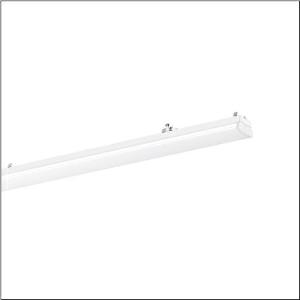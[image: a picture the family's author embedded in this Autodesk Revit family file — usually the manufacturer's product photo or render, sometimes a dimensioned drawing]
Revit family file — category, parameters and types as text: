
# Revit family: licross_r__11_recessed_opal_mo_51tl1d7n44xg_4ee8
name_source: partatom
category: Lighting Fixtures
units: mm (PartAtom-declared; Revit-internal decimal feet)

## family parameters
Cut with Voids When Loaded = No
Host = Face
Light Source = No
Part Type = Normal
Room Calculation Point = No
Round Connector Dimension = Use Diameter
Shared = No

## types (1)
- Licross® 11 recessed opal MO (1 x LED, 4480 lm, 24.8 W, 4000K)
    Apparent Load = 25 VA
    CIE Flux Codes = 44 73 91 87 100
    Color Rendering = 80
    Color Temperature = 4000K
    Default Elevation = 1800 mm
    Description = Licross® 11 recessed opal MO, luminaire insert, of sheet steel, coil coated, white, length: 1.500mm, width: 76mm, height: 87mm, LED rated luminous flux: 4.480lm, light colour: 840, control gear: ON/OFF, with plug, 3-pole, with phase selection, mains connection: 220..240V, AC, 50/60Hz, rated input power: 25W, halogen-free wiring, primary optical cover: cover, of PMMA, light emission: direct with ceiling illumination distribution, primary light characteristic: symmetric, protection rating (complete): IP40, insulation class (complete): insulation class I (protective earthing), certification: CE, ENEC, VDE, UKCA, protection symbol: D if used in an environment without relevant dust loads with corresponding accessories, impact resistance: IK06, permissible ambient temperature for indoor applications: -35..+45°C, corresponds to IFS (International Featured Standards) requirements for safety and quality in the food industry, reducing of maximum allowable ambient temperature of 5°C with ceiling mounting, packaging unit: 1 piece
    Height = 83 mm
    Lamp = 1 x LED
    Lamp Light Flux = 4480 lm
    Lamp Power = 24.8 W
    Lamp count = 1
    Length = 1500 mm
    Luminous efficacy = 181 lm/W
    Manufacturer = Siteco
    ModVariant = No
    Model = 51TL1D7N44XG
    Mounting Place = Ceiling
    Mounting Type = Pendant
    Number of Poles = 1
    OnlyDefault = Yes
    Power Factor = 1
    Product Name = Licross® 11 recessed opal MO
    Product group = luminaire insert
    ProductGroupID = 901
    Protection Class = Protection class I
    Protection Degree = IP 40
    RLX_Detail_Level = 1
    RLX_Emergency_Light_Flux = 0 lm
    RLX_Emergency_Type = 0
    RLX_Emergency_Type_DB = No
    RlxData = <blob elided: 23077 chars, md5=efe4834f>
    Socket = socket
    Standby Power = 0 W
    System Light Flux = 4480 lm
    System Power = 25 W
    Type Comments = Product without accessories
    Type Image = l_1313666.jpg
    URL = http://relux.com
    VarID = ---
    Voltage = 0 V
    Weight = 0.00 kg
    Width = 76 mm

## geometry (parser evidence)
native form markers: Blend x4, Sweep x11
no freeform markers — native parametric forms only
